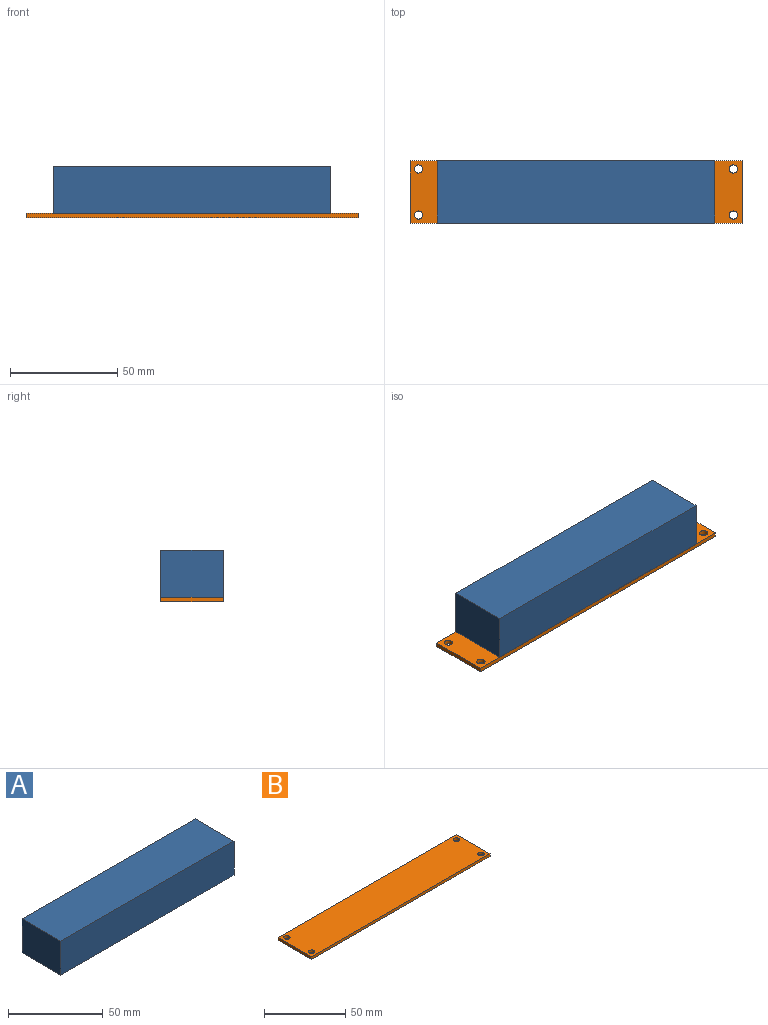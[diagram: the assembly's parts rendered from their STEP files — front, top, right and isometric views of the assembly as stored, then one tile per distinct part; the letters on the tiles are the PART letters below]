
ASSEMBLY  parts=2 mates=1
PART A: 6 faces, bbox 129.5x29x22 mm
  f0: plane 129.5x22mm, normal (0,-1,0), area 2849mm2, adj f1,f3,f4,f5
  f1: plane 29x22mm, normal (1,0,0), area 638mm2, adj f0,f2,f4,f5
  f2: plane 129.5x22mm, normal (0,1,0), area 2849mm2, adj f1,f3,f4,f5
  f3: plane 29x22mm, normal (-1,0,0), area 638mm2, adj f0,f2,f4,f5
  f4: plane 129.5x29mm, normal (0,0,1), area 3755.5mm2, adj f0,f1,f2,f3
  f5: plane 129.5x29mm, normal (0,0,-1), area 3755.5mm2, adj f0,f1,f2,f3
PART B: 10 faces, bbox 155x29x2 mm
  f0: plane 155x2mm, normal (0,-1,0), area 310mm2, adj f1,f6,f8,f9
  f1: plane 29x2mm, normal (1,0,0), area 58mm2, adj f0,f2,f8,f9
  f2: plane 155x2mm, normal (0,1,0), area 310mm2, adj f1,f6,f8,f9
  f3: cylinder r=1.9mm len=3.8mm, axis (0,0,-1), area 23.9mm2, adj f8,f9
  f4: cylinder r=1.9mm len=3.8mm, axis (0,0,-1), area 23.9mm2, adj f8,f9
  f5: cylinder r=1.9mm len=3.8mm, axis (0,0,-1), area 23.9mm2, adj f8,f9
  f6: plane 29x2mm, normal (-1,0,0), area 58mm2, adj f0,f2,f8,f9
  f7: cylinder r=1.9mm len=3.8mm, axis (0,0,-1), area 23.9mm2, adj f8,f9
  f8: plane 155x29mm, normal (0,0,1), area 4449.6mm2, adj f0,f1,f2,f3,f4,f5,f6,f7
  f9: plane 155x29mm, normal (0,0,-1), area 4449.6mm2, adj f0,f1,f2,f3,f4,f5,f6,f7
PLACE A t=(-28.05,-29.3,-32.66)mm
PLACE B t=(-28.05,-29.3,-32.66)mm
MATE fastened B.f8 <-> A.f5  axis (0,0,1) through (-28.05,-29.3,-30.66)mm
